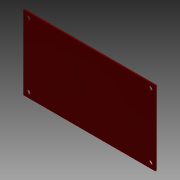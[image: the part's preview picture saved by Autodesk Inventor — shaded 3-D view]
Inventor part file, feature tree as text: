
AUTODESK INVENTOR PART (.ipt)
format: ipt  version: 2013 (Build 170138000, 138)  size: 108,544 bytes
history: native  units: in
note: dims shown in document units (in); Inventor stores cm internally (conversion verified against a paired STEP export)
features: extrude x1, sketch x1
ambient origin geometry x8: Origin, YZ Plane, XZ Plane, XY Plane, X Axis, Y Axis, Z Axis, Center Point
bodies: Solid1 (feature_tree)
feature tree (2):
  extrude  "Extrusion1"  Depth=4.0in
  sketch  "Sketch1"  dims[d0=0.0394in d1=0.0in d2=4.0in d4=2.25in d5=1.95in d6=0.1181in d7=3.7in]
